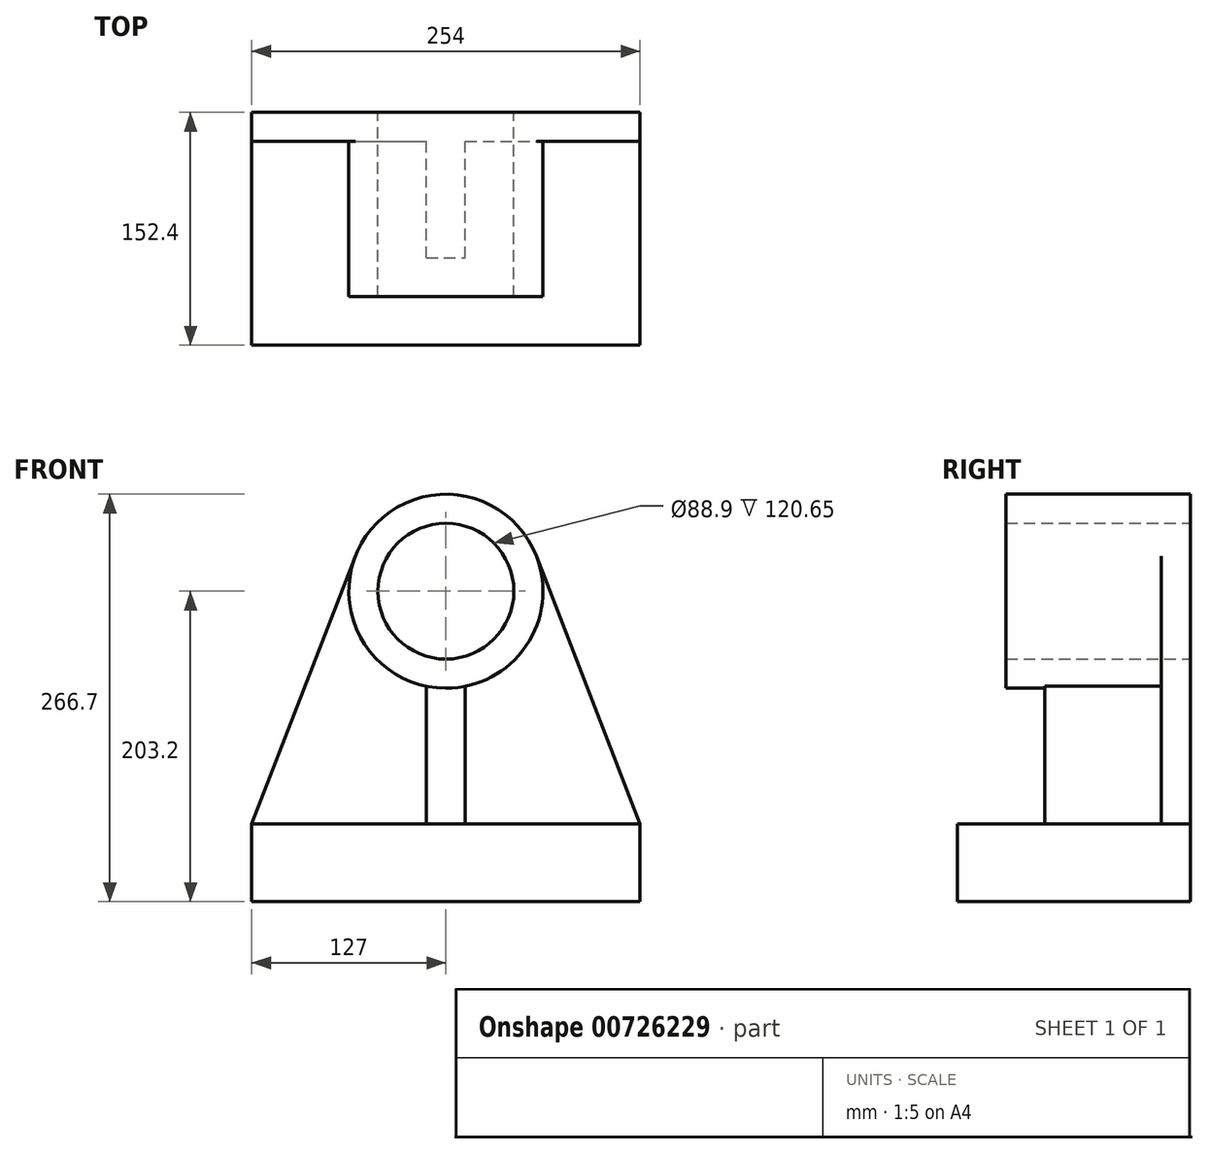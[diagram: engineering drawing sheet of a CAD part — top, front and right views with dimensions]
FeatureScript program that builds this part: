
annotation { "Feature Type Name" : "Feature", "Feature Type Description" : "" }
export const myFeature = defineFeature(function(context is Context, id is Id, definition is map)
    precondition{}
    {
        {
            var Q0;
            Q0=qCreatedBy(makeId("Front.planeOp"),FACE);
            var sketch = newSketch(context, id + "F0", { "sketchPlane" : qUnion([Q0])});
            skLineSegment(sketch, "E0", {"start": v(-137.7, 0) * mm, "end": v(116.3, 0) * mm});
            skLineSegment(sketch, "E1", {"start": v(116.3, 0) * mm, "end": v(116.3, 50.8) * mm});
            skLineSegment(sketch, "E2", {"start": v(116.3, 50.8) * mm, "end": v(48.53, 226.1) * mm});
            skLineSegment(sketch, "E3", {"start": v(-137.7, 0) * mm, "end": v(-137.7, 50.8) * mm});
            skLineSegment(sketch, "E4", {"start": v(-137.7, 50.8) * mm, "end": v(-69.93, 226.1) * mm});
            skArc(sketch, "E5", {"start": v(48.53, 226.1) * mm, "mid": v(-10.7, 266.7) * mm, "end": v(-69.93, 226.1) * mm});
            skCircle(sketch, "E6", {"center": v(-10.7, 203.2) * mm, "radius": 44.45 * mm});
            skSolve(sketch);
        }
        {
            var Q0;
            Q0 = qSketchRegion(id + "F0", true);
            extrude(context, id + "F1", {"entities" : qUnion([Q0]), "depth" : 19.05 * mm, "offsetDistance" : 25.4 * mm});
        }
        {
            var Q0;
            Q0=makeQuery(id+"F1.opExtrude","CAP_FACE",FACE,{"disambiguationData":[OSD([sQuery(id+"F0.wireOp",EDGE,"E0"),sQuery(id+"F0.wireOp",EDGE,"E1"),sQuery(id+"F0.wireOp",EDGE,"E2"),sQuery(id+"F0.wireOp",EDGE,"E3"),sQuery(id+"F0.wireOp",EDGE,"E4"),sQuery(id+"F0.wireOp",EDGE,"E5"),sQuery(id+"F0.wireOp",EDGE,"E6")])],"isStart":false});
            var sketch = newSketch(context, id + "F2", { "sketchPlane" : qUnion([Q0])});
            skLineSegment(sketch, "E7.bottom", {"start": v(-137.7, 0) * mm, "end": v(116.3, 0) * mm});
            skLineSegment(sketch, "E7.top", {"start": v(-137.7, 50.8) * mm, "end": v(116.3, 50.8) * mm});
            skLineSegment(sketch, "E7.left", {"start": v(-137.7, 0) * mm, "end": v(-137.7, 50.8) * mm});
            skLineSegment(sketch, "E7.right", {"start": v(116.3, 0) * mm, "end": v(116.3, 50.8) * mm});
            skSolve(sketch);
        }
        {
            var Q0;
            Q0 = qSketchRegion(id + "F2", true);
            extrude(context, id + "F3", {"entities" : qUnion([Q0]), "operationType" : NewBodyOperationType.ADD, "depth" : 133.35 * mm, "offsetDistance" : 25.4 * mm});
        }
        {
            var Q0;
            Q0=makeQuery(id+"F1.opExtrude","CAP_FACE",FACE,{"disambiguationData":[OSD([sQuery(id+"F0.wireOp",EDGE,"E0"),sQuery(id+"F0.wireOp",EDGE,"E1"),sQuery(id+"F0.wireOp",EDGE,"E2"),sQuery(id+"F0.wireOp",EDGE,"E3"),sQuery(id+"F0.wireOp",EDGE,"E4"),sQuery(id+"F0.wireOp",EDGE,"E5"),sQuery(id+"F0.wireOp",EDGE,"E6")])],"isStart":false});
            var sketch = newSketch(context, id + "F4", { "sketchPlane" : qUnion([Q0])});
            skCircle(sketch, "E8", {"center": v(-10.7, 203.2) * mm, "radius": 63.5 * mm});
            skCircle(sketch, "E9", {"center": v(-10.7, 203.2) * mm, "radius": 44.45 * mm});
            skSolve(sketch);
        }
        {
            var Q0;
            Q0 = qSketchRegion(id + "F4", true);
            extrude(context, id + "F5", {"entities" : qUnion([Q0]), "operationType" : NewBodyOperationType.ADD, "depth" : 101.6 * mm, "offsetDistance" : 25.4 * mm});
        }
        {
            var Q0;
            Q0=makeQuery(id+"F1.opExtrude","CAP_FACE",FACE,{"disambiguationData":[OSD([sQuery(id+"F0.wireOp",EDGE,"E0"),sQuery(id+"F0.wireOp",EDGE,"E1"),sQuery(id+"F0.wireOp",EDGE,"E2"),sQuery(id+"F0.wireOp",EDGE,"E3"),sQuery(id+"F0.wireOp",EDGE,"E4"),sQuery(id+"F0.wireOp",EDGE,"E5"),sQuery(id+"F0.wireOp",EDGE,"E6")])],"isStart":false});
            var sketch = newSketch(context, id + "F6", { "sketchPlane" : qUnion([Q0])});
            skLineSegment(sketch, "E10", {"start": v(2, 140.98) * mm, "end": v(2, 50.8) * mm});
            skLineSegment(sketch, "E11", {"start": v(-23.4, 140.98) * mm, "end": v(-23.4, 50.8) * mm});
            skSolve(sketch);
        }
        {
            var Q0;
            Q0 = qSketchRegion(id + "F6", true);
            var Q1;
            {var subQ0=sQuery(id+"F6.wireOp",EDGE,"E10");Q1=makeQuery(id+"F6.imprint","IMPRINT",FACE,{"disambiguationData":[TD([[makeQuery(id+"F6.imprint","IMPRINT",EDGE,{"derivedFrom":subQ0}),-1.0]])]});}
            extrude(context, id + "F7", {"entities" : qUnion([Q0, Q1]), "operationType" : NewBodyOperationType.ADD, "depth" : 76.2 * mm, "offsetDistance" : 25.4 * mm});
        }
    });
